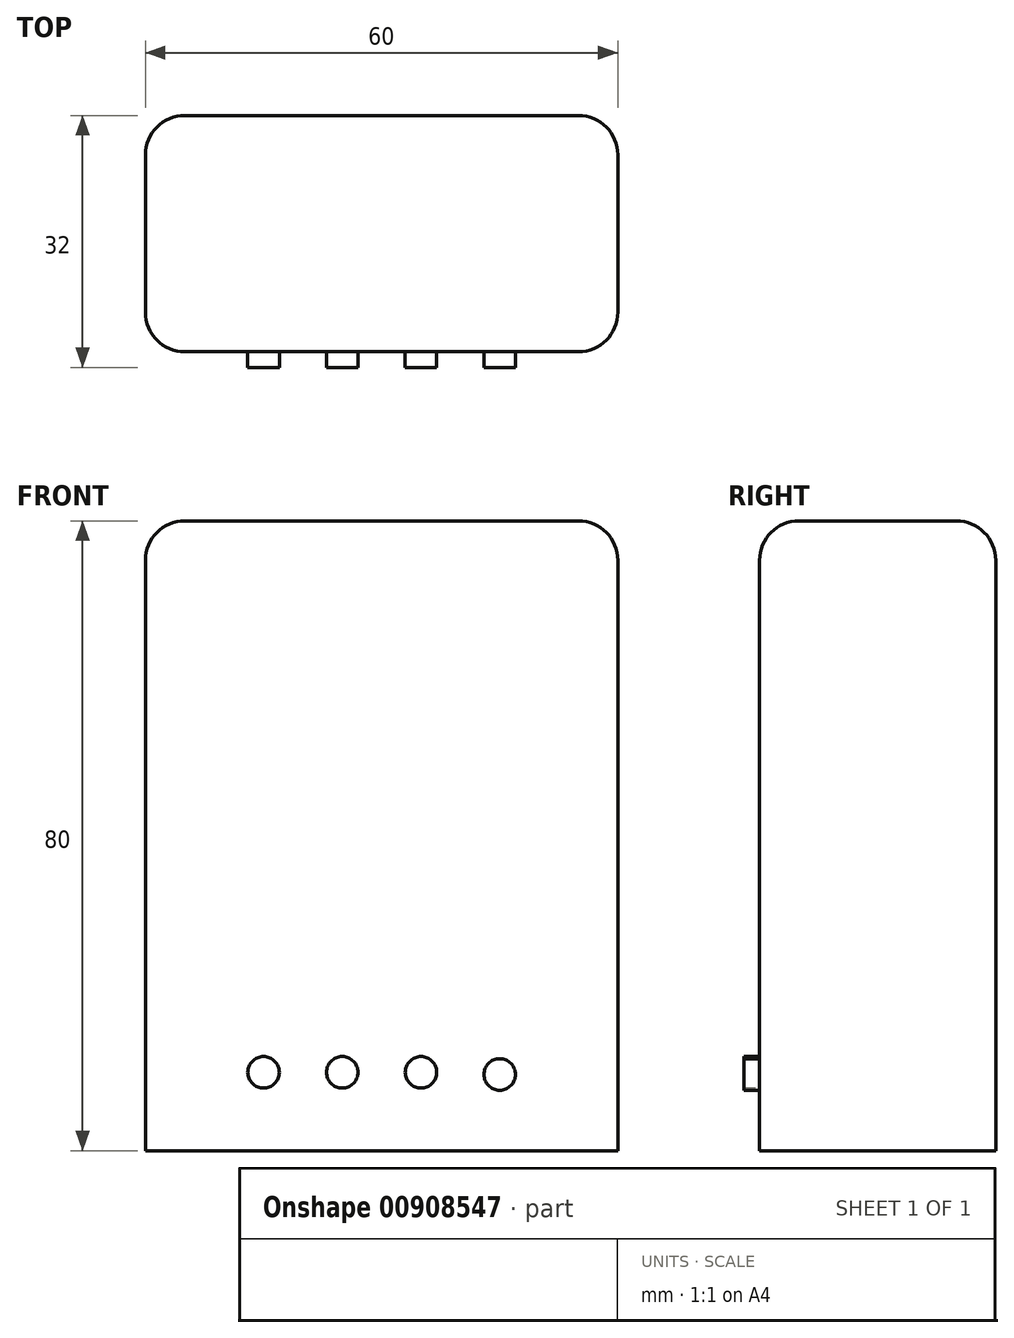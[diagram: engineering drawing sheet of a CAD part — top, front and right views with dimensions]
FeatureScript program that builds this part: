
annotation { "Feature Type Name" : "Feature", "Feature Type Description" : "" }
export const myFeature = defineFeature(function(context is Context, id is Id, definition is map)
    precondition{}
    {
        {
            var Q0;
            Q0=qCreatedBy(makeId("Front.planeOp"),FACE);
            var sketch = newSketch(context, id + "F0", { "sketchPlane" : qUnion([Q0])});
            skLineSegment(sketch, "E0.bottom", {"start": v(-30, 40) * mm, "end": v(30, 40) * mm});
            skLineSegment(sketch, "E0.top", {"start": v(-30, -40) * mm, "end": v(30, -40) * mm});
            skLineSegment(sketch, "E0.left", {"start": v(-30, 40) * mm, "end": v(-30, -40) * mm});
            skLineSegment(sketch, "E0.right", {"start": v(30, 40) * mm, "end": v(30, -40) * mm});
            skPoint(sketch, "E0.middle", {"position": v(0, 0) * mm});
            skCircle(sketch, "E1", {"center": v(-15, -30.05) * mm, "radius": 2 * mm});
            skCircle(sketch, "E2", {"center": v(15, -30.32) * mm, "radius": 2 * mm});
            skCircle(sketch, "E3", {"center": v(-5, -30.05) * mm, "radius": 2 * mm});
            skCircle(sketch, "E4", {"center": v(5, -30.05) * mm, "radius": 2 * mm});
            skSolve(sketch);
        }
        {
            var Q0;
            Q0=makeQuery(id+"F0.imprint","IMPRINT",FACE,{"disambiguationData":[TD([[makeQuery(id+"F0.imprint","IMPRINT",EDGE,{"derivedFrom":sQuery(id+"F0.wireOp",EDGE,"E0.bottom")}),-1.0]])]});
            extrude(context, id + "F1", {"entities" : qUnion([Q0]), "depth" : 30 * mm, "offsetDistance" : 25 * mm});
        }
        {
            var Q0;
            Q0=makeQuery(id+"F0.imprint","IMPRINT",FACE,{"disambiguationData":[TD([[makeQuery(id+"F0.imprint","IMPRINT",EDGE,{"derivedFrom":sQuery(id+"F0.wireOp",EDGE,"E1")}),1.0]])]});
            var Q1;
            Q1=makeQuery(id+"F0.imprint","IMPRINT",FACE,{"disambiguationData":[TD([[makeQuery(id+"F0.imprint","IMPRINT",EDGE,{"derivedFrom":sQuery(id+"F0.wireOp",EDGE,"p9CRhUao-WIYm-sOwl-DHlF-HO0xEFZ2aB1O")}),1.0]])]});
            var Q2;
            Q2=makeQuery(id+"F0.imprint","IMPRINT",FACE,{"disambiguationData":[TD([[makeQuery(id+"F0.imprint","IMPRINT",EDGE,{"derivedFrom":sQuery(id+"F0.wireOp",EDGE,"E2")}),1.0]])]});
            var Q3;
            Q3=makeQuery(id+"F0.imprint","IMPRINT",FACE,{"disambiguationData":[TD([[makeQuery(id+"F0.imprint","IMPRINT",EDGE,{"derivedFrom":sQuery(id+"F0.wireOp",EDGE,"E3")}),1.0]])]});
            var Q4;
            Q4=makeQuery(id+"F0.imprint","IMPRINT",FACE,{"disambiguationData":[TD([[makeQuery(id+"F0.imprint","IMPRINT",EDGE,{"derivedFrom":sQuery(id+"F0.wireOp",EDGE,"E4")}),1.0]])]});
            extrude(context, id + "F2", {"entities" : qUnion([Q0, Q1, Q2, Q3, Q4]), "operationType" : NewBodyOperationType.ADD, "depth" : 32 * mm, "offsetDistance" : 25 * mm});
        }
        {
            var Q0;
            Q0=makeQuery(id+"F1.opExtrude","CAP_EDGE",EDGE,{"disambiguationData":[OSD([sQuery(id+"F0.wireOp",EDGE,"E0.bottom")])],"isStart":false});
            var Q1;
            Q1=makeQuery(id+"F1.opExtrude","CAP_EDGE",EDGE,{"disambiguationData":[OSD([sQuery(id+"F0.wireOp",EDGE,"E0.bottom")])],"isStart":true});
            var Q2;
            Q2=makeQuery(id+"F1.opExtrude","SWEPT_EDGE",EDGE,{"disambiguationData":[OSD([sQuery(id+"F0.wireOp",EDGE,"E0.bottom"),sQuery(id+"F0.wireOp",EDGE,"E0.right")])]});
            var Q3;
            Q3=makeQuery(id+"F1.opExtrude","SWEPT_EDGE",EDGE,{"disambiguationData":[OSD([sQuery(id+"F0.wireOp",EDGE,"E0.bottom"),sQuery(id+"F0.wireOp",EDGE,"E0.left")])]});
            var Q4;
            Q4=makeQuery(id+"F1.opExtrude","CAP_EDGE",EDGE,{"disambiguationData":[OSD([sQuery(id+"F0.wireOp",EDGE,"E0.left")])],"isStart":false});
            var Q5;
            Q5=makeQuery(id+"F1.opExtrude","CAP_EDGE",EDGE,{"disambiguationData":[OSD([sQuery(id+"F0.wireOp",EDGE,"E0.right")])],"isStart":false});
            var Q6;
            Q6=makeQuery(id+"F1.opExtrude","CAP_EDGE",EDGE,{"disambiguationData":[OSD([sQuery(id+"F0.wireOp",EDGE,"E0.left")])],"isStart":true});
            var Q7;
            Q7=makeQuery(id+"F1.opExtrude","CAP_EDGE",EDGE,{"disambiguationData":[OSD([sQuery(id+"F0.wireOp",EDGE,"E0.right")])],"isStart":true});
            fillet(context, id + "F3", {"entities" : qUnion([Q0, Q1, Q2, Q3, Q4, Q5, Q6, Q7]), "radius" : 5 * mm, "tangentPropagation" : true, "allowEdgeOverflow" : false});
        }
    });
